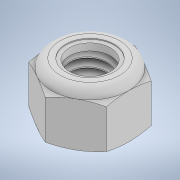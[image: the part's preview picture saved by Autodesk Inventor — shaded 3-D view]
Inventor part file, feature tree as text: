
AUTODESK INVENTOR PART (.ipt)
format: ipt  version: 2021 (Build 250183000, 183)  size: 374,784 bytes
history: native  units: in
note: dims shown in document units (in); Inventor stores cm internally (conversion verified against a paired STEP export)
features: revolve x1, boolean_combine x1
ambient origin geometry x8: Origin, YZ Plane, XZ Plane, XY Plane, X Axis, Y Axis, Z Axis, Center Point
bodies: Solid1 (feature_tree), Solid2 (feature_tree)
feature tree (2):
  revolve  "Revolve2"  [1 undecoded]
  boolean_combine  "Combine1"
note: 1 required parameter value undecoded (feature->parameter linkage not recoverable at this tier; creation-order binding heuristic only, values carry confidence <= 0.55)
